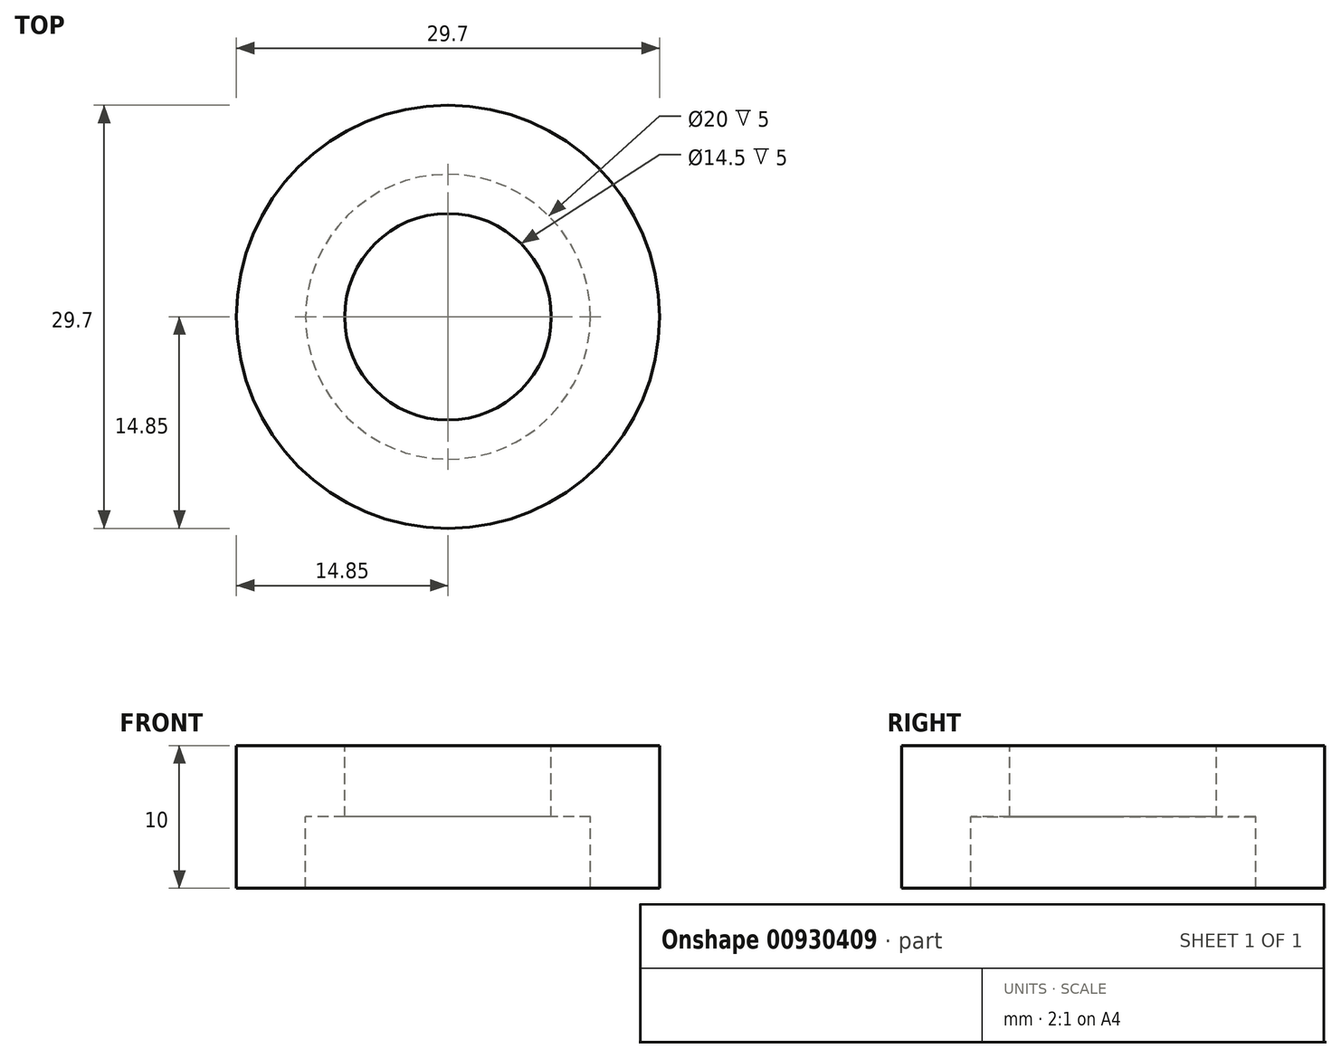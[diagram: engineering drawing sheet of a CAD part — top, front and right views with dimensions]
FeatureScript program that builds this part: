
annotation { "Feature Type Name" : "Feature", "Feature Type Description" : "" }
export const myFeature = defineFeature(function(context is Context, id is Id, definition is map)
    precondition{}
    {
        {
            var Q0;
            Q0=qCreatedBy(makeId("Front.planeOp"),FACE);
            var sketch = newSketch(context, id + "F0", { "sketchPlane" : qUnion([Q0])});
            skLineSegment(sketch, "E0", {"start": v(-10, -5) * mm, "end": v(-10, 0) * mm});
            skLineSegment(sketch, "E1", {"start": v(-10, 0) * mm, "end": v(-7.25, 0) * mm});
            skLineSegment(sketch, "E2", {"start": v(-7.25, 0) * mm, "end": v(-7.25, 5) * mm});
            skLineSegment(sketch, "E3", {"start": v(-7.25, 5) * mm, "end": v(-14.85, 5) * mm});
            skLineSegment(sketch, "E4", {"start": v(-14.85, 5) * mm, "end": v(-14.85, -5) * mm});
            skLineSegment(sketch, "E5", {"start": v(-14.85, -5) * mm, "end": v(-10, -5) * mm});
            skLineSegment(sketch, "E6", {"start": v(0, 42.47) * mm, "end": v(0, -22.77) * mm, "construction": true});
            skSolve(sketch);
        }
        {
            var Q0;
            Q0=makeQuery(id+"F0.imprint","IMPRINT",FACE,{"disambiguationData":[TD([[makeQuery(id+"F0.imprint","IMPRINT",EDGE,{"derivedFrom":sQuery(id+"F0.wireOp",EDGE,"E0")}),1.0]])]});
            var Q1;
            Q1=sQuery(id+"F0.wireOp",EDGE,"E6");
            revolve(context, id + "F1", {"surfaceOperationType" : NewSurfaceOperationType.NEW, "entities" : qUnion([Q0]), "axis" : qUnion([Q1]), "revolveType" : RevolveType.FULL});
        }
    });
